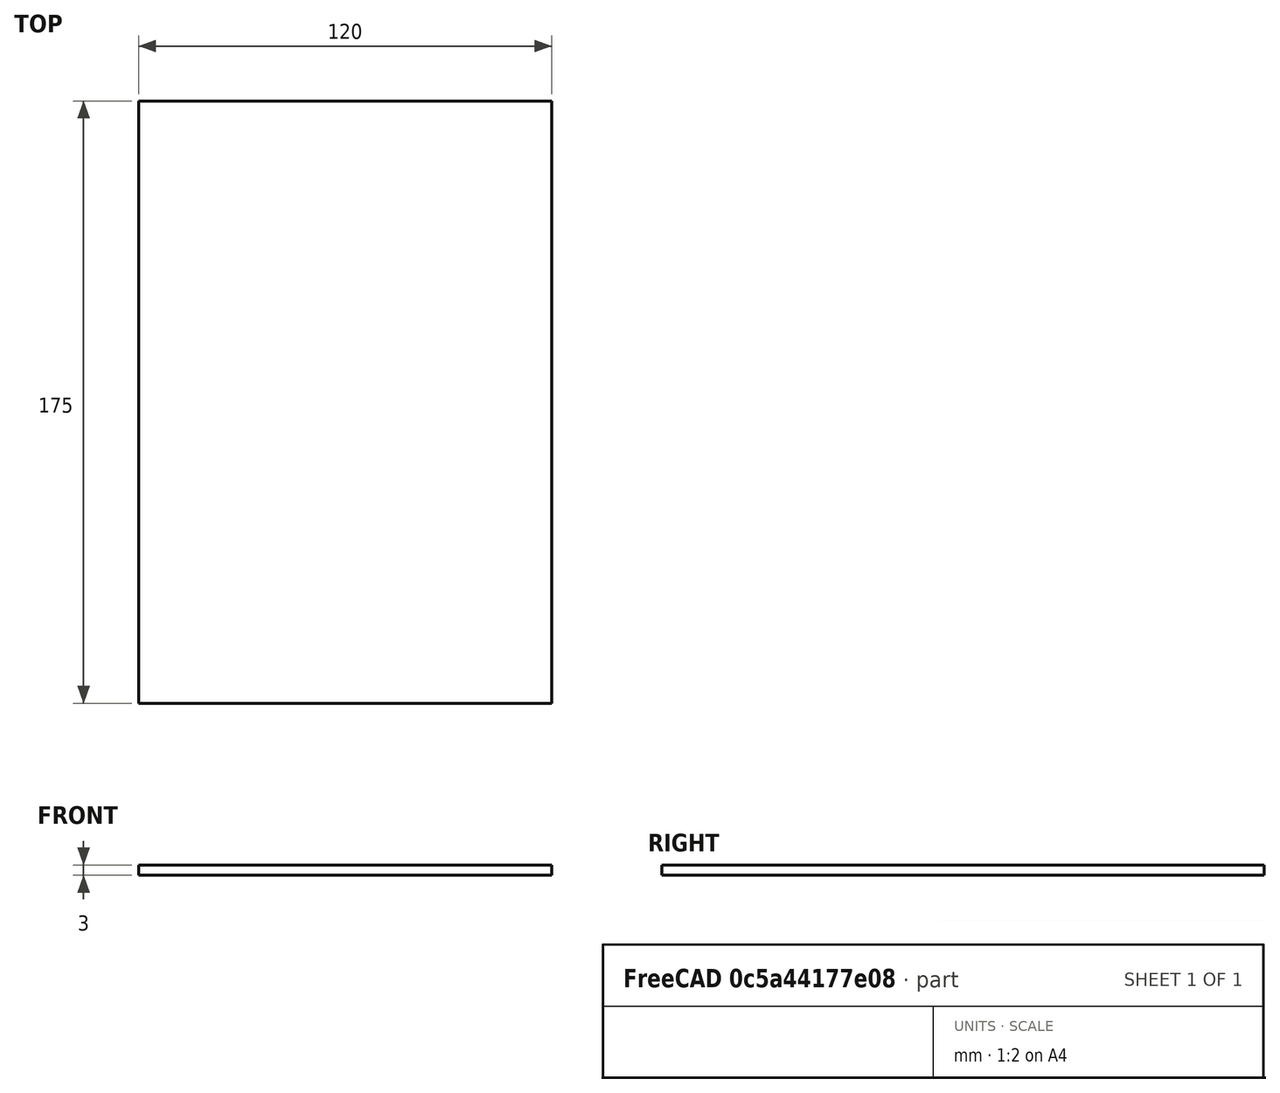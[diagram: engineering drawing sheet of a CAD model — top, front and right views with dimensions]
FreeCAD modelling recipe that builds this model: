
FCSTD DOCUMENT  (FreeCAD 0.19R23578 (Git))
Label: matrix_lamp_holder
License: All rights reserved
LicenseURL: http://en.wikipedia.org/wiki/All_rights_reserved
objects: Sketcher::SketchObject×2, PartDesign::Pad×1, PartDesign::Body×1
note: 5 computed .brp shape members not serialized (recipe doc carries the construction recipe); baked Part::Feature solids carry a one-line shape summary decoded from their .brp

FEATURE [Sketcher::SketchObject] Sketch
  MapMode = 5
  Support = -> [XY_Plane]
  sketch-geometry (4):
    g0: LineSegment StartX=-60 StartY=87.5 StartZ=0 EndX=60 EndY=87.5 EndZ=0
    g1: LineSegment StartX=60 StartY=87.5 StartZ=0 EndX=60 EndY=-87.5 EndZ=0
    g2: LineSegment StartX=60 StartY=-87.5 StartZ=0 EndX=-60 EndY=-87.5 EndZ=0
    g3: LineSegment StartX=-60 StartY=-87.5 StartZ=0 EndX=-60 EndY=87.5 EndZ=0
  constraints (10):
    c: Coincident(g0,g1)
    c: Coincident(g1,g2)
    c: Coincident(g2,g3)
    c: Coincident(g3,g0)
    c: Distance(g1) = 175
    c: Distance(g2) = 120
    c: Equal(g3,g1)
    c: Equal(g0,g2)
    c: Symmetric(g2,g0,g-1)
    c: Symmetric(g0,g0,g-2)
FEATURE [PartDesign::Pad] Pad
  Direction = (1,1,1)
  Length = 3
  Length2 = 100
  Profile = -> Sketch
  Type = 0
FEATURE [Sketcher::SketchObject] Sketch001
  MapMode = 5
  Placement = pos=(0,0,0) rot=(1,0,0;3.14159rad)
  Support = -> [Pad]
  sketch-geometry (1):
    g0: Circle CenterX=-22.4066 CenterY=66.4408 CenterZ=0 NormalX=0 NormalY=0 NormalZ=1 AngleXU=0 Radius=9.45034
FEATURE [PartDesign::Body] Body
  Group = -> [Sketch,Pad,Sketch001]
  Origin = -> Origin
  Tip = -> Pad
